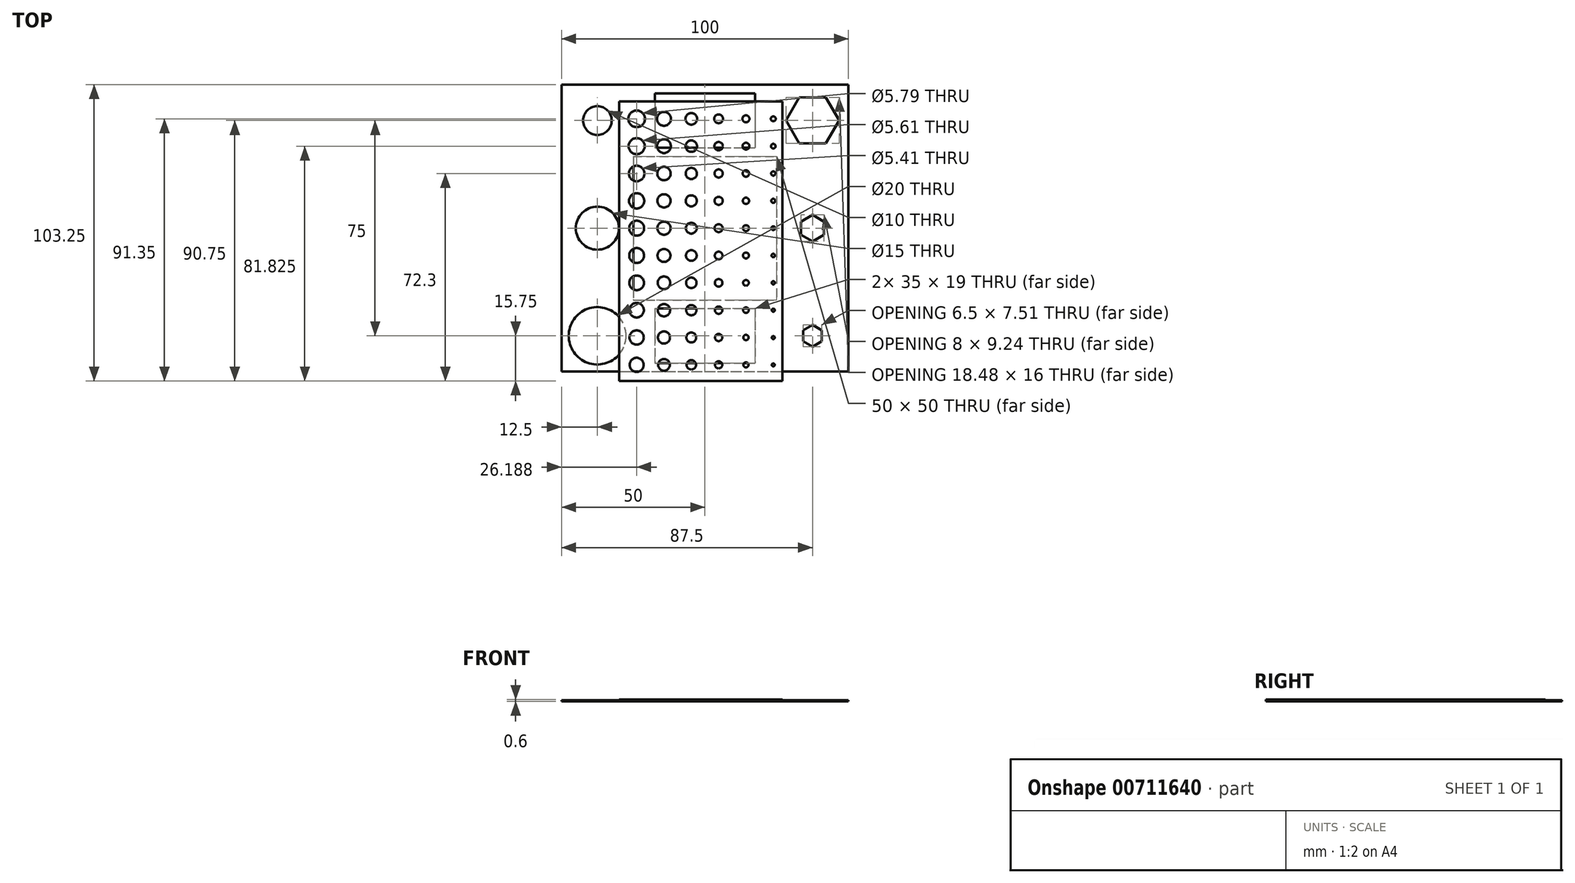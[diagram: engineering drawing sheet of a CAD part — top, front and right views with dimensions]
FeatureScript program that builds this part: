
annotation { "Feature Type Name" : "Feature", "Feature Type Description" : "" }
export const myFeature = defineFeature(function(context is Context, id is Id, definition is map)
    precondition{}
    {
        {
            var Q0;
            Q0=qCreatedBy(makeId("Top.planeOp"),FACE);
            var sketch = newSketch(context, id + "F0", { "sketchPlane" : qUnion([Q0])});
            skLineSegment(sketch, "E0.bottom", {"start": v(-50, 50) * mm, "end": v(50, 50) * mm});
            skLineSegment(sketch, "E0.top", {"start": v(-50, -50) * mm, "end": v(50, -50) * mm});
            skLineSegment(sketch, "E0.left", {"start": v(-50, 50) * mm, "end": v(-50, -50) * mm});
            skLineSegment(sketch, "E0.right", {"start": v(50, 50) * mm, "end": v(50, -50) * mm});
            skLineSegment(sketch, "E1.bottom", {"start": v(-25, 25) * mm, "end": v(25, 25) * mm});
            skLineSegment(sketch, "E1.top", {"start": v(-25, -25) * mm, "end": v(25, -25) * mm});
            skLineSegment(sketch, "E1.left", {"start": v(-25, 25) * mm, "end": v(-25, -25) * mm});
            skLineSegment(sketch, "E1.right", {"start": v(25, 25) * mm, "end": v(25, -25) * mm});
            skLineSegment(sketch, "E2", {"start": v(25, -25) * mm, "end": v(50, -50) * mm, "construction": true});
            skLineSegment(sketch, "E3", {"start": v(25, 25) * mm, "end": v(50, 50) * mm, "construction": true});
            skLineSegment(sketch, "E4", {"start": v(-25, 25) * mm, "end": v(-50, 50) * mm, "construction": true});
            skLineSegment(sketch, "E5", {"start": v(-50, -50) * mm, "end": v(-25, -25) * mm, "construction": true});
            skCircle(sketch, "E6", {"center": v(-37.5, -37.5) * mm, "radius": 10 * mm});
            skCircle(sketch, "E7", {"center": v(-37.5, 37.5) * mm, "radius": 5 * mm});
            skLineSegment(sketch, "E8", {"start": v(-37.5, 37.5) * mm, "end": v(-37.5, -37.5) * mm, "construction": true});
            skLineSegment(sketch, "E9", {"start": v(37.5, -37.5) * mm, "end": v(-37.5, -37.5) * mm, "construction": true});
            skLineSegment(sketch, "E10", {"start": v(37.5, -37.5) * mm, "end": v(37.5, 37.5) * mm, "construction": true});
            skLineSegment(sketch, "E11", {"start": v(37.5, 37.5) * mm, "end": v(-37.5, 37.5) * mm, "construction": true});
            skCircle(sketch, "E12", {"center": v(-37.5, 0) * mm, "radius": 7.5 * mm});
            skCircle(sketch, "E13.cCircle", {"center": v(37.5, -37.5) * mm, "radius": 3.25 * mm, "construction": true});
            skLineSegment(sketch, "E13.0", {"start": v(40.75, -35.62) * mm, "end": v(40.75, -39.38) * mm});
            skLineSegment(sketch, "E13.1", {"start": v(40.75, -39.38) * mm, "end": v(37.5, -41.25) * mm});
            skLineSegment(sketch, "E13.2", {"start": v(37.5, -41.25) * mm, "end": v(34.25, -39.38) * mm});
            skLineSegment(sketch, "E13.3", {"start": v(34.25, -39.38) * mm, "end": v(34.25, -35.62) * mm});
            skLineSegment(sketch, "E13.4", {"start": v(34.25, -35.62) * mm, "end": v(37.5, -33.75) * mm});
            skLineSegment(sketch, "E13.5", {"start": v(37.5, -33.75) * mm, "end": v(40.75, -35.62) * mm});
            skPoint(sketch, "E13.0.midPoint", {"position": v(40.75, -37.5) * mm});
            skCircle(sketch, "E14.cCircle", {"center": v(37.5, 0) * mm, "radius": 4 * mm, "construction": true});
            skLineSegment(sketch, "E14.0", {"start": v(41.5, 2.3) * mm, "end": v(41.5, -2.3) * mm});
            skLineSegment(sketch, "E14.1", {"start": v(41.5, -2.3) * mm, "end": v(37.5, -4.62) * mm});
            skLineSegment(sketch, "E14.2", {"start": v(37.5, -4.62) * mm, "end": v(33.5, -2.3) * mm});
            skLineSegment(sketch, "E14.3", {"start": v(33.5, -2.3) * mm, "end": v(33.5, 2.3) * mm});
            skLineSegment(sketch, "E14.4", {"start": v(33.5, 2.3) * mm, "end": v(37.5, 4.62) * mm});
            skLineSegment(sketch, "E14.5", {"start": v(37.5, 4.62) * mm, "end": v(41.5, 2.3) * mm});
            skPoint(sketch, "E14.0.midPoint", {"position": v(41.5, 0) * mm});
            skCircle(sketch, "E15.cCircle", {"center": v(37.5, 37.5) * mm, "radius": 8 * mm, "construction": true});
            skLineSegment(sketch, "E15.0", {"start": v(46.74, 37.5) * mm, "end": v(42.12, 29.5) * mm});
            skLineSegment(sketch, "E15.1", {"start": v(42.12, 29.5) * mm, "end": v(32.88, 29.5) * mm});
            skLineSegment(sketch, "E15.2", {"start": v(32.88, 29.5) * mm, "end": v(28.26, 37.5) * mm});
            skLineSegment(sketch, "E15.3", {"start": v(28.26, 37.5) * mm, "end": v(32.88, 45.5) * mm});
            skLineSegment(sketch, "E15.4", {"start": v(32.88, 45.5) * mm, "end": v(42.12, 45.5) * mm});
            skLineSegment(sketch, "E15.5", {"start": v(42.12, 45.5) * mm, "end": v(46.74, 37.5) * mm});
            skPoint(sketch, "E15.0.midPoint", {"position": v(44.43, 33.5) * mm});
            skLineSegment(sketch, "E16.bottom", {"start": v(-17.5, 47) * mm, "end": v(17.5, 47) * mm});
            skLineSegment(sketch, "E16.top", {"start": v(-17.5, 28) * mm, "end": v(17.5, 28) * mm});
            skLineSegment(sketch, "E16.left", {"start": v(-17.5, 47) * mm, "end": v(-17.5, 28) * mm});
            skLineSegment(sketch, "E16.right", {"start": v(17.5, 47) * mm, "end": v(17.5, 28) * mm});
            skLineSegment(sketch, "E17.bottom", {"start": v(-17.5, -28) * mm, "end": v(17.5, -28) * mm});
            skLineSegment(sketch, "E17.top", {"start": v(-17.5, -47) * mm, "end": v(17.5, -47) * mm});
            skLineSegment(sketch, "E17.left", {"start": v(-17.5, -28) * mm, "end": v(-17.5, -47) * mm});
            skLineSegment(sketch, "E17.right", {"start": v(17.5, -28) * mm, "end": v(17.5, -47) * mm});
            skSolve(sketch);
        }
        {
            var Q0;
            Q0=makeQuery(id+"F0.imprint","IMPRINT",FACE,{"disambiguationData":[TD([[makeQuery(id+"F0.imprint","IMPRINT",EDGE,{"derivedFrom":sQuery(id+"F0.wireOp",EDGE,"E0.bottom")}),-1.0]])]});
            extrude(context, id + "F1", {"entities" : qUnion([Q0]), "depth" : .35 * mm, "offsetDistance" : 25 * mm});
        }
        {
            var Q0;
            Q0=qCreatedBy(makeId("Top.planeOp"),FACE);
            var sketch = newSketch(context, id + "F2", { "sketchPlane" : qUnion([Q0])});
            skLineSegment(sketch, "E18.bottom", {"start": v(-23.81, 38.1) * mm, "end": v(-14.29, 38.1) * mm, "construction": true});
            skLineSegment(sketch, "E18.top", {"start": v(-23.81, 28.57) * mm, "end": v(-14.29, 28.57) * mm, "construction": true});
            skLineSegment(sketch, "E18.left", {"start": v(-23.81, 38.1) * mm, "end": v(-23.81, 28.57) * mm, "construction": true});
            skLineSegment(sketch, "E18.right", {"start": v(-14.29, 38.1) * mm, "end": v(-14.29, 28.58) * mm, "construction": true});
            skLineSegment(sketch, "E19", {"start": v(-23.81, 28.57) * mm, "end": v(-23.81, 19.05) * mm, "construction": true});
            skLineSegment(sketch, "E20", {"start": v(-23.81, 19.05) * mm, "end": v(-14.29, 19.05) * mm, "construction": true});
            skLineSegment(sketch, "E21", {"start": v(-14.29, 19.05) * mm, "end": v(-14.29, 28.57) * mm, "construction": true});
            skLineSegment(sketch, "E22", {"start": v(-23.81, 19.05) * mm, "end": v(-23.81, 9.52) * mm, "construction": true});
            skLineSegment(sketch, "E23", {"start": v(-23.81, 9.52) * mm, "end": v(-14.29, 9.52) * mm, "construction": true});
            skLineSegment(sketch, "E24", {"start": v(-14.29, 9.52) * mm, "end": v(-14.29, 19.05) * mm, "construction": true});
            skLineSegment(sketch, "E25", {"start": v(-23.81, 9.52) * mm, "end": v(-23.81, 0) * mm, "construction": true});
            skLineSegment(sketch, "E26", {"start": v(-23.81, 0) * mm, "end": v(-14.29, 0) * mm, "construction": true});
            skLineSegment(sketch, "E27", {"start": v(-14.29, 0) * mm, "end": v(-14.29, 9.52) * mm, "construction": true});
            skLineSegment(sketch, "E28", {"start": v(-23.81, 0) * mm, "end": v(-23.81, -9.52) * mm, "construction": true});
            skLineSegment(sketch, "E29", {"start": v(-23.81, -9.52) * mm, "end": v(-14.29, -9.52) * mm, "construction": true});
            skLineSegment(sketch, "E30", {"start": v(-14.29, -9.52) * mm, "end": v(-14.29, 0) * mm, "construction": true});
            skLineSegment(sketch, "E31", {"start": v(-23.81, -9.52) * mm, "end": v(-23.81, -19.05) * mm, "construction": true});
            skLineSegment(sketch, "E32", {"start": v(-23.81, -19.05) * mm, "end": v(-14.29, -19.05) * mm, "construction": true});
            skLineSegment(sketch, "E33", {"start": v(-14.29, -19.05) * mm, "end": v(-14.29, -9.52) * mm, "construction": true});
            skLineSegment(sketch, "E34", {"start": v(-23.81, -19.05) * mm, "end": v(-23.81, -28.57) * mm, "construction": true});
            skLineSegment(sketch, "E35", {"start": v(-23.81, -28.57) * mm, "end": v(-14.29, -28.57) * mm, "construction": true});
            skLineSegment(sketch, "E36", {"start": v(-14.29, -28.57) * mm, "end": v(-14.29, -19.05) * mm, "construction": true});
            skLineSegment(sketch, "E37", {"start": v(-23.81, -28.57) * mm, "end": v(-23.81, -38.1) * mm, "construction": true});
            skLineSegment(sketch, "E38", {"start": v(-23.81, -38.1) * mm, "end": v(-14.29, -38.1) * mm, "construction": true});
            skLineSegment(sketch, "E39", {"start": v(-14.29, -38.1) * mm, "end": v(-14.29, -28.57) * mm, "construction": true});
            skLineSegment(sketch, "E40", {"start": v(-14.29, 38.1) * mm, "end": v(-4.76, 38.1) * mm, "construction": true});
            skLineSegment(sketch, "E41", {"start": v(-4.76, 38.1) * mm, "end": v(-4.76, 28.57) * mm, "construction": true});
            skLineSegment(sketch, "E42", {"start": v(-4.76, 28.57) * mm, "end": v(-14.29, 28.57) * mm, "construction": true});
            skLineSegment(sketch, "E43", {"start": v(-4.76, 28.57) * mm, "end": v(-4.76, 19.05) * mm, "construction": true});
            skLineSegment(sketch, "E44", {"start": v(-4.76, 19.05) * mm, "end": v(-14.29, 19.05) * mm, "construction": true});
            skLineSegment(sketch, "E45", {"start": v(-4.76, 19.05) * mm, "end": v(-4.76, 9.52) * mm, "construction": true});
            skLineSegment(sketch, "E46", {"start": v(-4.76, 9.52) * mm, "end": v(-14.29, 9.52) * mm, "construction": true});
            skLineSegment(sketch, "E47", {"start": v(-4.76, 9.52) * mm, "end": v(-4.76, 0) * mm, "construction": true});
            skLineSegment(sketch, "E48", {"start": v(-4.76, 0) * mm, "end": v(-14.29, 0) * mm, "construction": true});
            skLineSegment(sketch, "E49", {"start": v(-4.76, 0) * mm, "end": v(-4.76, -9.52) * mm, "construction": true});
            skLineSegment(sketch, "E50", {"start": v(-4.76, -9.52) * mm, "end": v(-14.29, -9.52) * mm, "construction": true});
            skLineSegment(sketch, "E51", {"start": v(-4.76, -9.52) * mm, "end": v(-4.76, -19.05) * mm, "construction": true});
            skLineSegment(sketch, "E52", {"start": v(-4.76, -19.05) * mm, "end": v(-14.29, -19.05) * mm, "construction": true});
            skLineSegment(sketch, "E53", {"start": v(-4.76, -19.05) * mm, "end": v(-4.76, -28.57) * mm, "construction": true});
            skLineSegment(sketch, "E54", {"start": v(-4.76, -28.57) * mm, "end": v(-14.29, -28.57) * mm, "construction": true});
            skLineSegment(sketch, "E55", {"start": v(-4.76, -28.57) * mm, "end": v(-4.76, -38.1) * mm, "construction": true});
            skLineSegment(sketch, "E56", {"start": v(-4.76, -38.1) * mm, "end": v(-14.29, -38.1) * mm, "construction": true});
            skLineSegment(sketch, "E57", {"start": v(-4.76, 38.1) * mm, "end": v(4.76, 38.1) * mm, "construction": true});
            skLineSegment(sketch, "E58", {"start": v(4.76, 38.1) * mm, "end": v(4.76, 28.57) * mm, "construction": true});
            skLineSegment(sketch, "E59", {"start": v(4.76, 28.57) * mm, "end": v(-4.76, 28.57) * mm, "construction": true});
            skLineSegment(sketch, "E60", {"start": v(4.76, 28.57) * mm, "end": v(4.76, 19.05) * mm, "construction": true});
            skLineSegment(sketch, "E61", {"start": v(4.76, 19.05) * mm, "end": v(-4.76, 19.05) * mm, "construction": true});
            skLineSegment(sketch, "E62", {"start": v(4.76, 19.05) * mm, "end": v(4.76, 9.52) * mm, "construction": true});
            skLineSegment(sketch, "E63", {"start": v(4.76, 9.53) * mm, "end": v(-4.76, 9.52) * mm, "construction": true});
            skLineSegment(sketch, "E64", {"start": v(4.76, 9.52) * mm, "end": v(4.76, 0) * mm, "construction": true});
            skLineSegment(sketch, "E65", {"start": v(4.76, 0) * mm, "end": v(-4.76, 0) * mm, "construction": true});
            skLineSegment(sketch, "E66", {"start": v(4.76, 0) * mm, "end": v(4.76, -9.52) * mm, "construction": true});
            skLineSegment(sketch, "E67", {"start": v(4.76, -9.52) * mm, "end": v(-4.76, -9.52) * mm, "construction": true});
            skLineSegment(sketch, "E68", {"start": v(4.76, -9.52) * mm, "end": v(4.76, -19.05) * mm, "construction": true});
            skLineSegment(sketch, "E69", {"start": v(4.76, -19.05) * mm, "end": v(-4.76, -19.05) * mm, "construction": true});
            skLineSegment(sketch, "E70", {"start": v(4.76, -19.05) * mm, "end": v(4.76, -28.57) * mm, "construction": true});
            skLineSegment(sketch, "E71", {"start": v(4.76, -28.57) * mm, "end": v(-4.76, -28.57) * mm, "construction": true});
            skLineSegment(sketch, "E72", {"start": v(4.76, -28.57) * mm, "end": v(4.76, -38.1) * mm, "construction": true});
            skLineSegment(sketch, "E73", {"start": v(4.76, -38.1) * mm, "end": v(-4.76, -38.1) * mm, "construction": true});
            skLineSegment(sketch, "E74", {"start": v(4.76, 38.1) * mm, "end": v(14.29, 38.1) * mm, "construction": true});
            skLineSegment(sketch, "E75", {"start": v(14.29, 38.1) * mm, "end": v(14.29, 28.58) * mm, "construction": true});
            skLineSegment(sketch, "E76", {"start": v(14.29, 28.57) * mm, "end": v(4.76, 28.57) * mm, "construction": true});
            skLineSegment(sketch, "E77", {"start": v(14.29, 28.58) * mm, "end": v(14.29, 19.05) * mm, "construction": true});
            skLineSegment(sketch, "E78", {"start": v(14.29, 19.05) * mm, "end": v(4.76, 19.05) * mm, "construction": true});
            skLineSegment(sketch, "E79", {"start": v(14.29, 19.05) * mm, "end": v(14.29, 9.52) * mm, "construction": true});
            skLineSegment(sketch, "E80", {"start": v(14.29, 9.53) * mm, "end": v(4.76, 9.52) * mm, "construction": true});
            skLineSegment(sketch, "E81", {"start": v(14.29, 9.52) * mm, "end": v(14.29, 0) * mm, "construction": true});
            skLineSegment(sketch, "E82", {"start": v(14.29, 0) * mm, "end": v(4.76, 0) * mm, "construction": true});
            skLineSegment(sketch, "E83", {"start": v(14.29, 0) * mm, "end": v(14.29, -9.52) * mm, "construction": true});
            skLineSegment(sketch, "E84", {"start": v(14.29, -9.52) * mm, "end": v(4.76, -9.52) * mm, "construction": true});
            skLineSegment(sketch, "E85", {"start": v(14.29, -9.52) * mm, "end": v(14.29, -19.05) * mm, "construction": true});
            skLineSegment(sketch, "E86", {"start": v(14.29, -19.05) * mm, "end": v(4.76, -19.05) * mm, "construction": true});
            skLineSegment(sketch, "E87", {"start": v(14.29, -19.05) * mm, "end": v(14.29, -28.57) * mm, "construction": true});
            skLineSegment(sketch, "E88", {"start": v(14.29, -28.57) * mm, "end": v(4.76, -28.57) * mm, "construction": true});
            skLineSegment(sketch, "E89", {"start": v(14.29, -28.57) * mm, "end": v(14.29, -38.1) * mm, "construction": true});
            skLineSegment(sketch, "E90", {"start": v(14.29, -38.1) * mm, "end": v(4.76, -38.1) * mm, "construction": true});
            skLineSegment(sketch, "E91", {"start": v(14.29, 38.1) * mm, "end": v(23.81, 38.1) * mm, "construction": true});
            skLineSegment(sketch, "E92", {"start": v(23.81, 38.1) * mm, "end": v(23.81, 28.57) * mm, "construction": true});
            skLineSegment(sketch, "E93", {"start": v(23.81, 28.58) * mm, "end": v(14.29, 28.58) * mm, "construction": true});
            skLineSegment(sketch, "E94", {"start": v(23.81, 28.57) * mm, "end": v(23.81, 19.05) * mm, "construction": true});
            skLineSegment(sketch, "E95", {"start": v(23.81, 19.05) * mm, "end": v(14.29, 19.05) * mm, "construction": true});
            skLineSegment(sketch, "E96", {"start": v(23.81, 19.05) * mm, "end": v(23.81, 9.52) * mm, "construction": true});
            skLineSegment(sketch, "E97", {"start": v(23.81, 9.53) * mm, "end": v(14.29, 9.53) * mm, "construction": true});
            skLineSegment(sketch, "E98", {"start": v(23.81, 9.52) * mm, "end": v(23.81, 0) * mm, "construction": true});
            skLineSegment(sketch, "E99", {"start": v(23.81, 0) * mm, "end": v(14.29, 0) * mm, "construction": true});
            skLineSegment(sketch, "E100", {"start": v(23.81, 0) * mm, "end": v(23.81, -9.52) * mm, "construction": true});
            skLineSegment(sketch, "E101", {"start": v(23.81, -9.52) * mm, "end": v(14.29, -9.52) * mm, "construction": true});
            skLineSegment(sketch, "E102", {"start": v(23.81, -9.52) * mm, "end": v(23.81, -19.05) * mm, "construction": true});
            skLineSegment(sketch, "E103", {"start": v(23.81, -19.05) * mm, "end": v(14.29, -19.05) * mm, "construction": true});
            skLineSegment(sketch, "E104", {"start": v(23.81, -19.05) * mm, "end": v(23.81, -28.57) * mm, "construction": true});
            skLineSegment(sketch, "E105", {"start": v(23.81, -28.57) * mm, "end": v(14.29, -28.57) * mm, "construction": true});
            skLineSegment(sketch, "E106", {"start": v(23.81, -28.57) * mm, "end": v(23.81, -38.1) * mm, "construction": true});
            skLineSegment(sketch, "E107", {"start": v(23.81, -38.1) * mm, "end": v(14.29, -38.1) * mm, "construction": true});
            skLineSegment(sketch, "E108", {"start": v(-23.81, -38.1) * mm, "end": v(-23.81, -47.62) * mm, "construction": true});
            skLineSegment(sketch, "E109", {"start": v(-23.81, -47.62) * mm, "end": v(-14.29, -47.62) * mm, "construction": true});
            skLineSegment(sketch, "E110", {"start": v(-14.29, -47.62) * mm, "end": v(-14.29, -38.1) * mm, "construction": true});
            skLineSegment(sketch, "E111", {"start": v(-14.29, -47.62) * mm, "end": v(-4.76, -47.62) * mm, "construction": true});
            skLineSegment(sketch, "E112", {"start": v(-4.76, -47.62) * mm, "end": v(-4.76, -38.1) * mm, "construction": true});
            skLineSegment(sketch, "E113", {"start": v(-4.76, -47.62) * mm, "end": v(4.76, -47.62) * mm, "construction": true});
            skLineSegment(sketch, "E114", {"start": v(4.76, -47.62) * mm, "end": v(4.76, -38.1) * mm, "construction": true});
            skLineSegment(sketch, "E115", {"start": v(4.76, -47.62) * mm, "end": v(14.29, -47.62) * mm, "construction": true});
            skLineSegment(sketch, "E116", {"start": v(14.29, -47.62) * mm, "end": v(14.29, -38.1) * mm, "construction": true});
            skLineSegment(sketch, "E117", {"start": v(14.29, -47.62) * mm, "end": v(23.81, -47.62) * mm, "construction": true});
            skLineSegment(sketch, "E118", {"start": v(23.81, -47.62) * mm, "end": v(23.81, -38.1) * mm, "construction": true});
            skSolve(sketch);
        }
        {
            var Q0;
            Q0=qCreatedBy(makeId("Top.planeOp"),FACE);
            var sketch = newSketch(context, id + "F3", { "sketchPlane" : qUnion([Q0])});
            skCircle(sketch, "E119", {"center": v(-23.81, 38.1) * mm, "radius": 2.9 * mm});
            skCircle(sketch, "E120", {"center": v(-23.81, 28.57) * mm, "radius": 2.8 * mm});
            skCircle(sketch, "E121", {"center": v(-23.81, 19.05) * mm, "radius": 2.7 * mm});
            skCircle(sketch, "E122", {"center": v(-23.81, 9.52) * mm, "radius": 2.65 * mm});
            skCircle(sketch, "E123", {"center": v(-23.81, 0) * mm, "radius": 2.6 * mm});
            skCircle(sketch, "E124", {"center": v(-23.81, -9.52) * mm, "radius": 2.6 * mm});
            skCircle(sketch, "E125", {"center": v(-23.81, -19.05) * mm, "radius": 2.55 * mm});
            skCircle(sketch, "E126", {"center": v(-23.81, -28.57) * mm, "radius": 2.53 * mm});
            skCircle(sketch, "E127", {"center": v(-23.81, -38.1) * mm, "radius": 2.49 * mm});
            skCircle(sketch, "E128", {"center": v(-14.29, 38.1) * mm, "radius": 2.43 * mm});
            skCircle(sketch, "E129", {"center": v(-14.29, 28.58) * mm, "radius": 2.4 * mm});
            skCircle(sketch, "E130", {"center": v(-14.29, 19.05) * mm, "radius": 2.35 * mm});
            skCircle(sketch, "E131", {"center": v(-14.29, 9.52) * mm, "radius": 2.31 * mm});
            skCircle(sketch, "E132", {"center": v(-14.29, 0) * mm, "radius": 2.29 * mm});
            skCircle(sketch, "E133", {"center": v(-14.29, -9.52) * mm, "radius": 2.25 * mm});
            skCircle(sketch, "E134", {"center": v(-14.29, -19.05) * mm, "radius": 2.2 * mm});
            skCircle(sketch, "E135", {"center": v(-14.29, -28.57) * mm, "radius": 2.15 * mm});
            skCircle(sketch, "E136", {"center": v(-14.29, -38.1) * mm, "radius": 2.1 * mm});
            skCircle(sketch, "E137", {"center": v(-4.76, 38.1) * mm, "radius": 2.02 * mm});
            skCircle(sketch, "E138", {"center": v(-4.76, 28.57) * mm, "radius": 2 * mm});
            skCircle(sketch, "E139", {"center": v(-4.76, 19.05) * mm, "radius": 1.96 * mm});
            skCircle(sketch, "E140", {"center": v(-4.76, 9.52) * mm, "radius": 1.93 * mm});
            skCircle(sketch, "E141", {"center": v(-4.76, 0) * mm, "radius": 1.9 * mm});
            skCircle(sketch, "E142", {"center": v(-4.76, -9.52) * mm, "radius": 1.87 * mm});
            skCircle(sketch, "E143", {"center": v(-4.76, -19.05) * mm, "radius": 1.83 * mm});
            skCircle(sketch, "E144", {"center": v(-4.76, -28.57) * mm, "radius": 1.78 * mm});
            skCircle(sketch, "E145", {"center": v(-4.76, -38.1) * mm, "radius": 1.73 * mm});
            skCircle(sketch, "E146", {"center": v(4.76, 38.1) * mm, "radius": 1.52 * mm});
            skCircle(sketch, "E147", {"center": v(4.76, 28.57) * mm, "radius": 1.47 * mm});
            skCircle(sketch, "E148", {"center": v(4.76, 19.05) * mm, "radius": 1.44 * mm});
            skCircle(sketch, "E149", {"center": v(4.76, 9.52) * mm, "radius": 1.4 * mm});
            skCircle(sketch, "E150", {"center": v(4.76, 0) * mm, "radius": 1.4 * mm});
            skCircle(sketch, "E151", {"center": v(4.76, -9.52) * mm, "radius": 1.35 * mm});
            skCircle(sketch, "E152", {"center": v(4.76, -19.05) * mm, "radius": 1.32 * mm});
            skCircle(sketch, "E153", {"center": v(4.76, -28.57) * mm, "radius": 1.28 * mm});
            skCircle(sketch, "E154", {"center": v(4.76, -38.1) * mm, "radius": 1.26 * mm});
            skCircle(sketch, "E155", {"center": v(14.29, 38.1) * mm, "radius": 1.22 * mm});
            skCircle(sketch, "E156", {"center": v(14.29, 28.57) * mm, "radius": 1.18 * mm});
            skCircle(sketch, "E157", {"center": v(14.29, 19.05) * mm, "radius": 1.13 * mm});
            skCircle(sketch, "E158", {"center": v(14.29, 9.52) * mm, "radius": 1.1 * mm});
            skCircle(sketch, "E159", {"center": v(14.29, 0) * mm, "radius": 1.04 * mm});
            skCircle(sketch, "E160", {"center": v(14.29, -9.52) * mm, "radius": 1.03 * mm});
            skCircle(sketch, "E161", {"center": v(14.29, -19.05) * mm, "radius": 1 * mm});
            skCircle(sketch, "E162", {"center": v(14.29, -28.57) * mm, "radius": 0.97 * mm});
            skCircle(sketch, "E163", {"center": v(14.29, -38.1) * mm, "radius": 0.93 * mm});
            skCircle(sketch, "E164", {"center": v(23.81, 38.1) * mm, "radius": 0.85 * mm});
            skCircle(sketch, "E165", {"center": v(23.81, 28.58) * mm, "radius": 0.8 * mm});
            skCircle(sketch, "E166", {"center": v(23.81, 19.05) * mm, "radius": 0.75 * mm});
            skCircle(sketch, "E167", {"center": v(23.81, 9.53) * mm, "radius": 0.7 * mm});
            skCircle(sketch, "E168", {"center": v(23.81, 0) * mm, "radius": 0.66 * mm});
            skCircle(sketch, "E169", {"center": v(23.81, -9.52) * mm, "radius": 0.58 * mm});
            skCircle(sketch, "E170", {"center": v(23.81, -19.05) * mm, "radius": 0.55 * mm});
            skCircle(sketch, "E171", {"center": v(23.81, -28.57) * mm, "radius": 0.53 * mm});
            skCircle(sketch, "E172", {"center": v(23.81, -38.1) * mm, "radius": 0.52 * mm});
            skCircle(sketch, "E173", {"center": v(-23.81, -47.62) * mm, "radius": 2.45 * mm});
            skCircle(sketch, "E174", {"center": v(-14.29, -47.62) * mm, "radius": 2.04 * mm});
            skCircle(sketch, "E175", {"center": v(-4.76, -47.62) * mm, "radius": 1.63 * mm});
            skCircle(sketch, "E176", {"center": v(4.76, -47.62) * mm, "radius": 1.24 * mm});
            skCircle(sketch, "E177", {"center": v(14.29, -47.62) * mm, "radius": 0.89 * mm});
            skCircle(sketch, "E178", {"center": v(23.81, -47.62) * mm, "radius": 0.5 * mm});
            skLineSegment(sketch, "E179.bottom", {"start": v(-29.88, 44.17) * mm, "end": v(26.99, 44.17) * mm});
            skLineSegment(sketch, "E179.top", {"start": v(-29.88, -53.25) * mm, "end": v(26.99, -53.25) * mm});
            skLineSegment(sketch, "E179.left", {"start": v(-29.88, 44.17) * mm, "end": v(-29.88, -53.25) * mm});
            skLineSegment(sketch, "E179.right", {"start": v(26.99, 44.17) * mm, "end": v(26.99, -53.25) * mm});
            skSolve(sketch);
        }
        {
            var Q0;
            Q0=makeQuery(id+"F3.imprint","IMPRINT",FACE,{"disambiguationData":[TD([[makeQuery(id+"F3.imprint","IMPRINT",EDGE,{"derivedFrom":sQuery(id+"F3.wireOp",EDGE,"E119")}),-1.0]])]});
            extrude(context, id + "F4", {"entities" : qUnion([Q0]), "flatOperationType" : FlatOperationType.REMOVE, "thickness1" : 6.35 * mm, "thickness2" : 0 * mm, "thickness" : 6.35 * mm, "depth" : 0.6 * mm, "offsetDistance" : 25.4 * mm, "startOffsetBound" : StartOffsetType.BLIND, "startOffsetDistance" : 25.4 * mm, "domain" : OperationDomain.MODEL});
        }
    });
